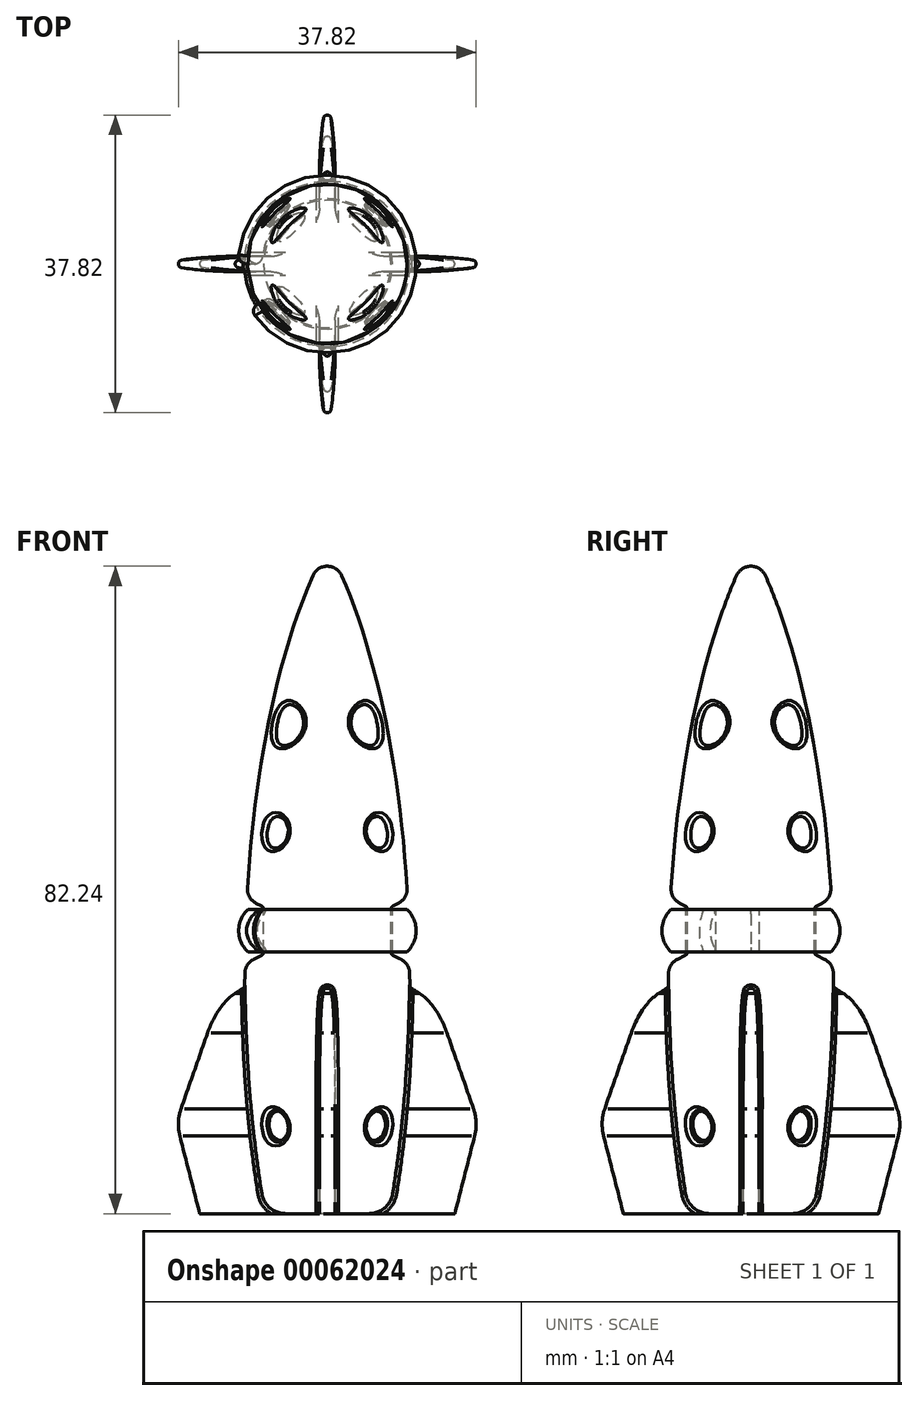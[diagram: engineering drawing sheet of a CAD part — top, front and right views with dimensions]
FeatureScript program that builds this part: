
annotation { "Feature Type Name" : "Feature", "Feature Type Description" : "" }
export const myFeature = defineFeature(function(context is Context, id is Id, definition is map)
    precondition{}
    {
        {
            var Q0;
            Q0=qCreatedBy(makeId("Front.planeOp"),FACE);
            var sketch = newSketch(context, id + "F0", { "sketchPlane" : qUnion([Q0])});
            skEllipticalArc(sketch, "E0", {});
            skLineSegment(sketch, "E1", {"start": v(0, 54.98) * mm, "end": v(0, -29.78) * mm});
            skLineSegment(sketch, "E2", {"start": v(0, -29.78) * mm, "end": v(-8, -29.78) * mm});
            skLineSegment(sketch, "E3", {"start": v(0, 0) * mm, "end": v(12, 0) * mm, "construction": true});
            skEllipticalArc(sketch, "E4.MirrorCS", {});
            skLineSegment(sketch, "E5.MirrorCS", {"start": v(0, -29.78) * mm, "end": v(8, -29.78) * mm});
            skPoint(sketch, "E6.visualSharp", {"position": v(0, 54.98) * mm});
            skArc(sketch, "E6.filletArc", {"start": v(1.83, 51.28) * mm, "mid": v(0, 52.46) * mm, "end": v(-1.83, 51.28) * mm});
            skEllipticalArc(sketch, "E7", {});
            skLineSegment(sketch, "E8", {"start": v(-15, -29.78) * mm, "end": v(-8, -29.78) * mm});
            skLineSegment(sketch, "E9", {"start": v(-8, -13) * mm, "end": v(-8, 0) * mm, "construction": true});
            skPoint(sketch, "E9.endSnap0", {"position": v(-8, -1) * mm});
            skLineSegment(sketch, "E10", {"start": v(-8, 0) * mm, "end": v(0, 0) * mm, "construction": true});
            skLineSegment(sketch, "E11", {"start": v(-10.5, -1.79) * mm, "end": v(-7.76, 0) * mm});
            skPoint(sketch, "E12", {"position": v(-7.76, 0) * mm});
            skLineSegment(sketch, "E13", {"start": v(-10.38, 6.67) * mm, "end": v(0, 6.67) * mm, "construction": true});
            skEllipticalArc(sketch, "E14.trimOffspring", {});
            skLineSegment(sketch, "E15", {"start": v(-14, -6.82) * mm, "end": v(-17.37, -16.44) * mm});
            skPoint(sketch, "E16.start.orphan", {"position": v(-15, -13) * mm});
            skLineSegment(sketch, "E17", {"start": v(-15, -29.78) * mm, "end": v(-17.52, -19.9) * mm});
            skPoint(sketch, "E18.visualSharp", {"position": v(-17.97, -18.15) * mm});
            skArc(sketch, "E18.filletArc", {"start": v(-17.37, -16.44) * mm, "mid": v(-17.7, -18.16) * mm, "end": v(-17.52, -19.9) * mm});
            skLineSegment(sketch, "E19", {"start": v(-9.02, 9.64) * mm, "end": v(-8.35, 9.32) * mm});
            skLineSegment(sketch, "E20", {"start": v(-9.34, 2.55) * mm, "end": v(-8.35, 3.03) * mm});
            skLineSegment(sketch, "E21", {"start": v(-10.5, -1.79) * mm, "end": v(-10.46, 0.77) * mm});
            skLineSegment(sketch, "E22", {"start": v(-8.07, 8.87) * mm, "end": v(-8.07, 3.48) * mm});
            skPoint(sketch, "E23.visualSharp", {"position": v(-10.22, 10.22) * mm});
            skArc(sketch, "E23.filletArc", {"start": v(-10.14, 11.56) * mm, "mid": v(-9.87, 10.43) * mm, "end": v(-9.02, 9.64) * mm});
            skPoint(sketch, "E24.visualSharp", {"position": v(-10.45, 2) * mm});
            skArc(sketch, "E24.filletArc", {"start": v(-9.34, 2.55) * mm, "mid": v(-10.15, 1.82) * mm, "end": v(-10.46, 0.77) * mm});
            skPoint(sketch, "E25.visualSharp", {"position": v(-8.07, 9.18) * mm});
            skArc(sketch, "E25.filletArc", {"start": v(-8.07, 8.87) * mm, "mid": v(-8.15, 9.13) * mm, "end": v(-8.35, 9.32) * mm});
            skPoint(sketch, "E26.visualSharp", {"position": v(-8.07, 3.16) * mm});
            skArc(sketch, "E26.filletArc", {"start": v(-8.35, 3.03) * mm, "mid": v(-8.15, 3.21) * mm, "end": v(-8.07, 3.48) * mm});
            skLineSegment(sketch, "E27", {"start": v(-8.07, 8.87) * mm, "end": v(-8.27, 8.87) * mm, "construction": true});
            skLineSegment(sketch, "E28", {"start": v(-8.07, 3.48) * mm, "end": v(-8.27, 3.48) * mm, "construction": true});
            skLineSegment(sketch, "E29", {"start": v(-8.27, 8.87) * mm, "end": v(-8.27, 3.48) * mm});
            skLineSegment(sketch, "E30", {"start": v(-8.27, 8.87) * mm, "end": v(-10.15, 8.87) * mm});
            skLineSegment(sketch, "E31", {"start": v(-10.15, 8.87) * mm, "end": v(-10.15, 3.48) * mm, "construction": true});
            skLineSegment(sketch, "E32", {"start": v(-10.15, 3.48) * mm, "end": v(-8.27, 3.48) * mm});
            skArc(sketch, "E33", {"start": v(-10.15, 8.87) * mm, "mid": v(-11.3, 6.17) * mm, "end": v(-10.15, 3.48) * mm});
            const initialGuessF0  = {"E0": [0.012, 0, 0, 1, 0.065, 0.0225, 0.6618337746130242, 1.391935060083807], "E4.MirrorCS": [-0.012, 0, 0, 1, 0.065, 0.0225, 4.236506730724271, 5.621351532566562], "E7": [-0.008, -0.013, 0, 1, 0.012, 0.007, 0.36390848754049565, 1.030244949723588], "E14.trimOffspring": [0.012, 0, 0, 1, 0.065, 0.0225, 1.5982743409528373, 2.046678576455316]};
            skSetInitialGuess(sketch, initialGuessF0);
            skSolve(sketch);
        }
        {
            var Q0;
            {var subQ0=sQuery(id+"F0.wireOp",EDGE,"E2");Q0=makeQuery(id+"F0.imprint","IMPRINT",FACE,{"disambiguationData":[TD([[makeQuery(id+"F0.imprint","IMPRINT",EDGE,{"derivedFrom":subQ0}),-1.0]])]});}
            var Q1;
            {var subQ0=sQuery(id+"F0.wireOp",EDGE,"2d9Q3B8T-FTmL-3iQ1-Mkdo-XyoXu4Tp89Yh");Q1=makeQuery(id+"F0.imprint","IMPRINT",FACE,{"disambiguationData":[TD([[makeQuery(id+"F0.imprint","IMPRINT",EDGE,{"derivedFrom":subQ0}),-1.0]])]});}
            var Q2;
            {var subQ3=sQuery(id+"F0.wireOp",EDGE,"LQuKZnSh-e9vf-0Ous-Bipi-XbTucNrK9EHz");Q2=makeQuery(id+"F0.imprint","IMPRINT",FACE,{"disambiguationData":[TD([[makeQuery(id+"F0.imprint","IMPRINT",EDGE,{"derivedFrom":subQ3}),-1.0]])]});}
            var Q3;
            Q3=sQuery(id+"F0.wireOp",EDGE,"E1");
            revolve(context, id + "F1", {"entities" : qUnion([Q0, Q1, Q2]), "axis" : qUnion([Q3]), "revolveType" : RevolveType.FULL});
        }
        {
            var Q0;
            Q0=makeQuery(id+"F1.opRevolve","SWEPT_FACE",FACE,{"disambiguationData":[OSD([sQuery(id+"F0.wireOp",EDGE,"E2")])]});
            var sketch = newSketch(context, id + "F2", { "sketchPlane" : qUnion([Q0])});
            skEllipticalArc(sketch, "E34", {});
            skLineSegment(sketch, "E35", {"start": v(-8, 2) * mm, "end": v(0, 2) * mm, "construction": true});
            skLineSegment(sketch, "E36", {"start": v(0, 2) * mm, "end": v(0, 0) * mm, "construction": true});
            skLineSegment(sketch, "E37", {"start": v(-18.43, 0) * mm, "end": v(2.43, 0) * mm});
            skEllipticalArc(sketch, "E38.MirrorCS", {});
            skPoint(sketch, "E39.visualSharp", {"position": v(-18.43, 0) * mm});
            skArc(sketch, "E39.filletArc", {"start": v(-15.77, 0.5) * mm, "mid": v(-16.2, 0) * mm, "end": v(-15.77, -0.5) * mm});
            const initialGuessF2  = {"E34": [-0.008, 0.002, -1, 0, 0.014, 0.003, 0.9820781024828917, 2.411864997362827], "E38.MirrorCS": [-0.008, -0.002, -1, 0, 0.014, 0.003, 3.8713203098167592, 5.301107204696695]};
            skSetInitialGuess(sketch, initialGuessF2);
            skSolve(sketch);
        }
        {
            var Q0;
            Q0=qSketchRegion(id+"F2",true);
            var Q1;
            Q1=sQuery(id+"F0.wireOp",EDGE,"E17");
            var Q2;
            Q2=sQuery(id+"F0.wireOp",EDGE,"E18.filletArc");
            var Q3;
            Q3=sQuery(id+"F0.wireOp",EDGE,"E15");
            var Q4;
            Q4=sQuery(id+"F0.wireOp",EDGE,"E7");
            var Q5;
            Q5=sQuery(id+"F0.wireOp",EDGE,"E11");
            sweep(context, id + "F3", {"profiles" : qUnion([Q0]), "path" : qUnion([Q1, Q2, Q3, Q4, Q5]), "keepProfileOrientation" : true});
        }
        {
            var Q0;
            Q0=makeQuery(id+"F3.opSweep","SWEPT_BODY",BODY,{"disambiguationData":[OSD([sQuery(id+"F0.wireOp",EDGE,"E11"),sQuery(id+"F2.wireOp",EDGE,"E34"),sQuery(id+"F2.wireOp",EDGE,"E38.MirrorCS"),sQuery(id+"F2.wireOp",EDGE,"E39.filletArc")])]});
            var Q1;
            Q1=sQuery(id+"F0.wireOp",EDGE,"E1");
            circularPattern(context, id + "F4", {"operationType" : NewBodyOperationType.ADD, "entities" : qUnion([Q0]), "axis" : qUnion([Q1]), "angle" : 360 * degree, "instanceCount" : round(4), "equalSpace" : true});
        }
        {
            var Q0;
            Q0=makeQuery(id+"F1.opRevolve","SWEPT_EDGE",EDGE,{"disambiguationData":[OSD([sQuery(id+"F0.wireOp",EDGE,"E0"),sQuery(id+"F0.wireOp",EDGE,"28322ec1-41a0-472d-8e85-a561dd0ad4dd")])]});
            var Q1;
            Q1=makeQuery(id+"F1.opRevolve","SWEPT_EDGE",EDGE,{"disambiguationData":[OSD([sQuery(id+"F0.wireOp",EDGE,"28322ec1-41a0-472d-8e85-a561dd0ad4dd"),sQuery(id+"F0.wireOp",EDGE,"E14.trimOffspring")])]});
            fillet(context, id + "F5", {"entities" : qUnion([Q0, Q1]), "radius" : 3 * mm, "tangentPropagation" : true, "allowEdgeOverflow" : false});
        }
        {
            var Q0;
            Q0=qCreatedBy(makeId("Front.planeOp"),FACE);
            var sketch = newSketch(context, id + "F6", { "sketchPlane" : qUnion([Q0])});
            skLineSegment(sketch, "E40", {"start": v(-8.57, 18.6) * mm, "end": v(-8.76, 16.74) * mm});
            skLineSegment(sketch, "E41", {"start": v(-8.76, 16.74) * mm, "end": v(-9.75, 16.6) * mm});
            skLineSegment(sketch, "E42", {"start": v(-8.57, 18.6) * mm, "end": v(-16.64, 19.44) * mm});
            skLineSegment(sketch, "E43", {"start": v(-16.64, 19.44) * mm, "end": v(-9.75, 16.6) * mm});
            skLineSegment(sketch, "E44", {"start": v(-16.5, 34.4) * mm, "end": v(-7.93, 29.64) * mm});
            skLineSegment(sketch, "E45", {"start": v(-7.93, 29.64) * mm, "end": v(-6.78, 29.86) * mm});
            skLineSegment(sketch, "E46", {"start": v(-6.78, 29.86) * mm, "end": v(-6.35, 32.06) * mm});
            skLineSegment(sketch, "E47", {"start": v(-16.5, 34.4) * mm, "end": v(-6.35, 32.06) * mm});
            skSolve(sketch);
        }
        {
            var Q0;
            Q0=makeQuery(id+"F6.imprint","IMPRINT",FACE,{"disambiguationData":[TD([[makeQuery(id+"F6.imprint","IMPRINT",EDGE,{"derivedFrom":sQuery(id+"F6.wireOp",EDGE,"E44")}),1.0]])]});
            var Q1;
            Q1=sQuery(id+"F6.wireOp",EDGE,"E47");
            revolve(context, id + "F7", {"entities" : qUnion([Q0]), "axis" : qUnion([Q1]), "revolveType" : RevolveType.FULL, "oppositeDirection" : true});
        }
        {
            var Q0;
            Q0=makeQuery(id+"F6.imprint","IMPRINT",FACE,{"disambiguationData":[TD([[makeQuery(id+"F6.imprint","IMPRINT",EDGE,{"derivedFrom":sQuery(id+"F6.wireOp",EDGE,"E40")}),-1.0]])]});
            var Q1;
            Q1=sQuery(id+"F6.wireOp",EDGE,"E42");
            revolve(context, id + "F8", {"entities" : qUnion([Q0]), "axis" : qUnion([Q1]), "revolveType" : RevolveType.FULL, "oppositeDirection" : true});
        }
        {
            var Q0;
            Q0=makeQuery(id+"F7.opRevolve","SWEPT_BODY",BODY,{"disambiguationData":[OSD([sQuery(id+"F6.wireOp",EDGE,"E44"),sQuery(id+"F6.wireOp",EDGE,"E45"),sQuery(id+"F6.wireOp",EDGE,"E46"),sQuery(id+"F6.wireOp",EDGE,"E47")])]});
            var Q1;
            Q1=makeQuery(id+"F8.opRevolve","SWEPT_BODY",BODY,{"disambiguationData":[OSD([sQuery(id+"F6.wireOp",EDGE,"E40"),sQuery(id+"F6.wireOp",EDGE,"E41"),sQuery(id+"F6.wireOp",EDGE,"E42"),sQuery(id+"F6.wireOp",EDGE,"E43")])]});
            var Q2;
            Q2=sQuery(id+"F0.wireOp",EDGE,"E1");
            circularPattern(context, id + "F9", {"entities" : qUnion([Q0, Q1]), "axis" : qUnion([Q2]), "angle" : 45 * degree, "instanceCount" : 2});
        }
        {
            var Q0;
            Q0=makeQuery(id+"F9.opPattern","COPY",BODY,{"derivedFrom":makeQuery(id+"F8.opRevolve","SWEPT_BODY",BODY,{"disambiguationData":[OSD([sQuery(id+"F6.wireOp",EDGE,"E40"),sQuery(id+"F6.wireOp",EDGE,"E41"),sQuery(id+"F6.wireOp",EDGE,"E42"),sQuery(id+"F6.wireOp",EDGE,"E43")])]}),"instanceName":"1"});
            var Q1;
            Q1=makeQuery(id+"F9.opPattern","COPY",BODY,{"derivedFrom":makeQuery(id+"F7.opRevolve","SWEPT_BODY",BODY,{"disambiguationData":[OSD([sQuery(id+"F6.wireOp",EDGE,"E44"),sQuery(id+"F6.wireOp",EDGE,"E45"),sQuery(id+"F6.wireOp",EDGE,"E46"),sQuery(id+"F6.wireOp",EDGE,"E47")])]}),"instanceName":"1"});
            var Q2;
            Q2=sQuery(id+"F0.wireOp",EDGE,"E1");
            circularPattern(context, id + "F10", {"operationType" : NewBodyOperationType.REMOVE, "entities" : qUnion([Q0, Q1]), "axis" : qUnion([Q2]), "angle" : 90 * degree, "instanceCount" : 4});
        }
        {
            var Q0;
            Q0=makeQuery(id+"F1.opRevolve","SWEPT_FACE",FACE,{"disambiguationData":[OSD([sQuery(id+"F0.wireOp",EDGE,"E0")])]});
            fillet(context, id + "F11", {"entities" : qUnion([Q0]), "radius" : 0.5 * mm, "tangentPropagation" : true, "allowEdgeOverflow" : false});
        }
        {
            var Q0;
            Q0=makeQuery(id+"F10.boolean.opBoolean","COPY",FACE,{"derivedFrom":makeQuery(id+"F10.opPattern","COPY",FACE,{"derivedFrom":makeQuery(id+"F9.opPattern","COPY",FACE,{"derivedFrom":makeQuery(id+"F7.opRevolve","SWEPT_FACE",FACE,{"disambiguationData":[OSD([sQuery(id+"F6.wireOp",EDGE,"E46")])]}),"instanceName":"1"}),"instanceName":"3"})});
            var Q1;
            Q1=makeQuery(id+"F10.boolean.opBoolean","COPY",FACE,{"derivedFrom":makeQuery(id+"F10.opPattern","COPY",FACE,{"derivedFrom":makeQuery(id+"F9.opPattern","COPY",FACE,{"derivedFrom":makeQuery(id+"F8.opRevolve","SWEPT_FACE",FACE,{"disambiguationData":[OSD([sQuery(id+"F6.wireOp",EDGE,"E40")])]}),"instanceName":"1"}),"instanceName":"3"})});
            var Q2;
            Q2=makeQuery(id+"F10.boolean.opBoolean","COPY",FACE,{"derivedFrom":makeQuery(id+"F9.opPattern","COPY",FACE,{"derivedFrom":makeQuery(id+"F7.opRevolve","SWEPT_FACE",FACE,{"disambiguationData":[OSD([sQuery(id+"F6.wireOp",EDGE,"E46")])]}),"instanceName":"1"})});
            var Q3;
            Q3=makeQuery(id+"F10.boolean.opBoolean","COPY",FACE,{"derivedFrom":makeQuery(id+"F9.opPattern","COPY",FACE,{"derivedFrom":makeQuery(id+"F8.opRevolve","SWEPT_FACE",FACE,{"disambiguationData":[OSD([sQuery(id+"F6.wireOp",EDGE,"E40")])]}),"instanceName":"1"})});
            var Q4;
            Q4=makeQuery(id+"F10.boolean.opBoolean","COPY",FACE,{"derivedFrom":makeQuery(id+"F10.opPattern","COPY",FACE,{"derivedFrom":makeQuery(id+"F9.opPattern","COPY",FACE,{"derivedFrom":makeQuery(id+"F7.opRevolve","SWEPT_FACE",FACE,{"disambiguationData":[OSD([sQuery(id+"F6.wireOp",EDGE,"E46")])]}),"instanceName":"1"}),"instanceName":"2"})});
            var Q5;
            Q5=makeQuery(id+"F10.boolean.opBoolean","COPY",FACE,{"derivedFrom":makeQuery(id+"F10.opPattern","COPY",FACE,{"derivedFrom":makeQuery(id+"F9.opPattern","COPY",FACE,{"derivedFrom":makeQuery(id+"F8.opRevolve","SWEPT_FACE",FACE,{"disambiguationData":[OSD([sQuery(id+"F6.wireOp",EDGE,"E40")])]}),"instanceName":"1"}),"instanceName":"2"})});
            var Q6;
            Q6=makeQuery(id+"F10.boolean.opBoolean","COPY",FACE,{"derivedFrom":makeQuery(id+"F10.opPattern","COPY",FACE,{"derivedFrom":makeQuery(id+"F9.opPattern","COPY",FACE,{"derivedFrom":makeQuery(id+"F7.opRevolve","SWEPT_FACE",FACE,{"disambiguationData":[OSD([sQuery(id+"F6.wireOp",EDGE,"E46")])]}),"instanceName":"1"}),"instanceName":"1"})});
            var Q7;
            Q7=makeQuery(id+"F10.boolean.opBoolean","COPY",FACE,{"derivedFrom":makeQuery(id+"F10.opPattern","COPY",FACE,{"derivedFrom":makeQuery(id+"F9.opPattern","COPY",FACE,{"derivedFrom":makeQuery(id+"F8.opRevolve","SWEPT_FACE",FACE,{"disambiguationData":[OSD([sQuery(id+"F6.wireOp",EDGE,"E40")])]}),"instanceName":"1"}),"instanceName":"1"})});
            fillet(context, id + "F12", {"entities" : qUnion([Q0, Q1, Q2, Q3, Q4, Q5, Q6, Q7]), "radius" : 0.25 * mm, "tangentPropagation" : true, "allowEdgeOverflow" : false});
        }
        {
            var Q0;
            Q0=makeQuery(id+"F8.opRevolve","SWEPT_BODY",BODY,{"disambiguationData":[OSD([sQuery(id+"F6.wireOp",EDGE,"E40"),sQuery(id+"F6.wireOp",EDGE,"E41"),sQuery(id+"F6.wireOp",EDGE,"E42"),sQuery(id+"F6.wireOp",EDGE,"E43")])]});
            var Q1;
            Q1=qCreatedBy(makeId("Top.planeOp"),FACE);
            mirror(context, id + "F13", {"entities" : qUnion([Q0]), "mirrorPlane" : qUnion([Q1])});
        }
        {
            var Q0;
            Q0=makeQuery(id+"F13.opPattern","COPY",BODY,{"derivedFrom":makeQuery(id+"F8.opRevolve","SWEPT_BODY",BODY,{"disambiguationData":[OSD([sQuery(id+"F6.wireOp",EDGE,"E40"),sQuery(id+"F6.wireOp",EDGE,"E41"),sQuery(id+"F6.wireOp",EDGE,"E42"),sQuery(id+"F6.wireOp",EDGE,"E43")])]}),"instanceName":"1"});
            var Q1;
            Q1=sQuery(id+"F0.wireOp",EDGE,"E1");
            circularPattern(context, id + "F14", {"entities" : qUnion([Q0]), "axis" : qUnion([Q1]), "angle" : 45 * degree, "instanceCount" : 2});
        }
        {
            var Q0;
            Q0=makeQuery(id+"F14.opPattern","COPY",BODY,{"derivedFrom":makeQuery(id+"F13.opPattern","COPY",BODY,{"derivedFrom":makeQuery(id+"F8.opRevolve","SWEPT_BODY",BODY,{"disambiguationData":[OSD([sQuery(id+"F6.wireOp",EDGE,"E40"),sQuery(id+"F6.wireOp",EDGE,"E41"),sQuery(id+"F6.wireOp",EDGE,"E42"),sQuery(id+"F6.wireOp",EDGE,"E43")])]}),"instanceName":"1"}),"instanceName":"1"});
            var Q1;
            Q1=sQuery(id+"F0.wireOp",EDGE,"E1");
            circularPattern(context, id + "F15", {"operationType" : NewBodyOperationType.REMOVE, "entities" : qUnion([Q0]), "axis" : qUnion([Q1]), "angle" : 90 * degree, "instanceCount" : 4});
        }
        {
            var Q0;
            {var subQ1=sQuery(id+"F2.wireOp",EDGE,"E34");var subQ5=sQuery(id+"F0.wireOp",EDGE,"E7");Q0=makeQuery(id+"F4.boolean.opBoolean","SPLIT",FACE,{"disambiguationData":[TD([makeQuery(id+"F4.opPattern","COPY",FACE,{"derivedFrom":makeQuery(id+"F3.opSweep","SWEPT_FACE",FACE,{"disambiguationData":[OSD([subQ5,subQ1])]}),"instanceName":"1"})])],"derivedFrom":makeQuery(id+"F1.opRevolve","SWEPT_FACE",FACE,{"disambiguationData":[OSD([sQuery(id+"F0.wireOp",EDGE,"E14.trimOffspring")])]})});}
            var Q1;
            {var subQ1=sQuery(id+"F2.wireOp",EDGE,"E34");var subQ5=sQuery(id+"F0.wireOp",EDGE,"E7");Q1=makeQuery(id+"F4.boolean.opBoolean","SPLIT",FACE,{"disambiguationData":[TD([makeQuery(id+"F3.opSweep","SWEPT_FACE",FACE,{"disambiguationData":[OSD([subQ5,subQ1])]})])],"derivedFrom":makeQuery(id+"F1.opRevolve","SWEPT_FACE",FACE,{"disambiguationData":[OSD([sQuery(id+"F0.wireOp",EDGE,"E14.trimOffspring")])]})});}
            var Q2;
            {var subQ0=sQuery(id+"F2.wireOp",EDGE,"E34");var subQ7=sQuery(id+"F0.wireOp",EDGE,"E7");Q2=makeQuery(id+"F4.boolean.opBoolean","SPLIT",FACE,{"disambiguationData":[TD([makeQuery(id+"F4.opPattern","COPY",FACE,{"derivedFrom":makeQuery(id+"F3.opSweep","SWEPT_FACE",FACE,{"disambiguationData":[OSD([subQ7,subQ0])]}),"instanceName":"2"})])],"derivedFrom":makeQuery(id+"F1.opRevolve","SWEPT_FACE",FACE,{"disambiguationData":[OSD([sQuery(id+"F0.wireOp",EDGE,"E14.trimOffspring")])]})});}
            var Q3;
            {var subQ0=sQuery(id+"F2.wireOp",EDGE,"E38.MirrorCS");var subQ7=sQuery(id+"F0.wireOp",EDGE,"E7");Q3=makeQuery(id+"F4.boolean.opBoolean","SPLIT",FACE,{"disambiguationData":[TD([makeQuery(id+"F3.opSweep","SWEPT_FACE",FACE,{"disambiguationData":[OSD([subQ7,subQ0])]})])],"derivedFrom":makeQuery(id+"F1.opRevolve","SWEPT_FACE",FACE,{"disambiguationData":[OSD([sQuery(id+"F0.wireOp",EDGE,"E14.trimOffspring")])]})});}
            fillet(context, id + "F16", {"entities" : qUnion([Q0, Q1, Q2, Q3]), "radius" : 0.5 * mm, "tangentPropagation" : true, "allowEdgeOverflow" : false});
        }
        {
            var Q0;
            Q0=makeQuery(id+"F0.imprint","IMPRINT",FACE,{"disambiguationData":[TD([[makeQuery(id+"F0.imprint","IMPRINT",EDGE,{"derivedFrom":sQuery(id+"F0.wireOp",EDGE,"E29")}),-1.0]])]});
            var Q1;
            Q1=sQuery(id+"F0.wireOp",EDGE,"E33");
            var Q2;
            Q2=sQuery(id+"F0.wireOp",EDGE,"E30");
            var Q3;
            Q3=sQuery(id+"F0.wireOp",EDGE,"E29");
            var Q4;
            Q4=sQuery(id+"F0.wireOp",EDGE,"E32");
            var Q5;
            Q5=sQuery(id+"F0.wireOp",EDGE,"E1");
            revolve(context, id + "F17", {"entities" : qUnion([Q0]), "surfaceEntities" : qUnion([Q1, Q2, Q3, Q4]), "axis" : qUnion([Q5]), "revolveType" : RevolveType.ONE_DIRECTION, "angle" : 330 * degree});
        }
        {
            var Q0;
            Q0=makeQuery(id+"F17.opRevolve","CAP_EDGE",EDGE,{"disambiguationData":[OSD([sQuery(id+"F0.wireOp",EDGE,"E33")])],"isStart":true});
            var Q1;
            Q1=makeQuery(id+"F17.opRevolve","CAP_EDGE",EDGE,{"disambiguationData":[OSD([sQuery(id+"F0.wireOp",EDGE,"E29")])],"isStart":true});
            var Q2;
            Q2=makeQuery(id+"F17.opRevolve","CAP_EDGE",EDGE,{"disambiguationData":[OSD([sQuery(id+"F0.wireOp",EDGE,"E33")])],"isStart":false});
            var Q3;
            Q3=makeQuery(id+"F17.opRevolve","CAP_EDGE",EDGE,{"disambiguationData":[OSD([sQuery(id+"F0.wireOp",EDGE,"E29")])],"isStart":false});
            fillet(context, id + "F18", {"entities" : qUnion([Q0, Q1, Q2, Q3]), "radius" : 1 * mm, "tangentPropagation" : true, "allowEdgeOverflow" : false});
        }
        {
            var Q0;
            Q0=makeQuery(id+"F7.opRevolve","SWEPT_BODY",BODY,{"disambiguationData":[OSD([sQuery(id+"F6.wireOp",EDGE,"E44"),sQuery(id+"F6.wireOp",EDGE,"E45"),sQuery(id+"F6.wireOp",EDGE,"E46"),sQuery(id+"F6.wireOp",EDGE,"E47")])]});
            deleteBodies(context, id + "F19", {"entities" : qUnion([Q0])});
        }
        {
            var Q0;
            Q0=makeQuery(id+"F8.opRevolve","SWEPT_BODY",BODY,{"disambiguationData":[OSD([sQuery(id+"F6.wireOp",EDGE,"E40"),sQuery(id+"F6.wireOp",EDGE,"E41"),sQuery(id+"F6.wireOp",EDGE,"E42"),sQuery(id+"F6.wireOp",EDGE,"E43")])]});
            deleteBodies(context, id + "F20", {"entities" : qUnion([Q0])});
        }
        {
            var Q0;
            Q0=makeQuery(id+"F13.opPattern","COPY",BODY,{"derivedFrom":makeQuery(id+"F8.opRevolve","SWEPT_BODY",BODY,{"disambiguationData":[OSD([sQuery(id+"F6.wireOp",EDGE,"E40"),sQuery(id+"F6.wireOp",EDGE,"E41"),sQuery(id+"F6.wireOp",EDGE,"E42"),sQuery(id+"F6.wireOp",EDGE,"E43")])]}),"instanceName":"1"});
            deleteBodies(context, id + "F21", {"entities" : qUnion([Q0])});
        }
    });
